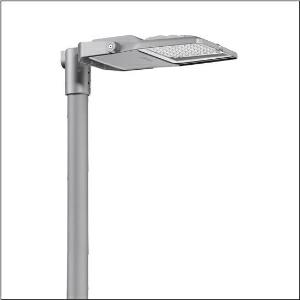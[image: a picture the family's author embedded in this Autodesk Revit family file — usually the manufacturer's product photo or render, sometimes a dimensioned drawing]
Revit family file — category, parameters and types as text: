
# Revit family: floodlight_fl_21_iq_mini___pl33t_5xa7772b4f3a_8cfb
name_source: partatom
category: Lighting Fixtures
units: mm (PartAtom-declared; Revit-internal decimal feet)

## family parameters
Cut with Voids When Loaded = No
Host = Face
Light Source = No
Part Type = Normal
Room Calculation Point = No
Round Connector Dimension = Use Diameter
Shared = No

## types (1)
- --- (1 x LED, 6420 lm, 45.5 W, 4000K)
    Apparent Load = 46 VA
    CIE Flux Codes = 26 75 99 100 100
    Color Rendering = 70
    Color Temperature = 4000K
    Default Elevation = 1800 mm
    Description = Floodlight FL 21 iQ mini, floodlight, primary light control with lens, of PMMA, primary optical cover: protective disc, of toughened safety glass, transparent, light distribution: PL33T, light emission: direct distribution, installation type: surface-mounted, LED, High Power LED, rated luminous flux: 6.420lm, luminous efficacy: 141lm/W, light colour: 740, colour temperature: 4000K, control: Auto-Match, Temp-Guard, Night-Set, Smart-Wire, Desk-Remote (wireless, voltage-free reading and setting of iQ features in the workshop via application-optimized NFC function/RFID function), optimised constant luminous flux control (CLO 2.0), Light-Fading, Lumen-Switch, with terminal, 6-pole, mains connection: 220..240V, AC, 50/60Hz, start of lifetime: 46W, end of service life: 48W, reduction: 22W, luminaire housing, of diecast aluminium, powder-coated, Siteco® metallic grey (DB 702S), corrosivity category C5 mid according to DIN EN ISO 12944, sealing non-destructively replaceable, please order mast flange separately, mast bracket, of steel, galvanised, powder-coated, protection rating (complete): IP66, insulation class (complete): insulation class II (safety insulation), certification: CE, ENEC, VDE, protection symbol: D, impact resistance: IK08, permissible operating ambient temperature: -40..+40°C, permissible operating ambient temperature for outdoor applications: -40..+50°C, standard: DIN EN 12944, LABS conformity tested according to VDMA 24364:2018-05, packaging unit: 1 piece

Light Distribution: PL33T
    Height = 70 mm
    Lamp = 1 x LED
    Lamp Light Flux = 6420 lm
    Lamp Power = 45.5 W
    Lamp count = 1
    Length = 485 mm
    Luminous efficacy = 141 lm/W
    Manufacturer = Siteco
    ModVariant = No
    Model = 5XA7772B4F3A
    Number of Poles = 1
    OnlyDefault = Yes
    Power Factor = 1
    Product Name = Floodlight FL 21 iQ mini | PL33T
    Product group = floodlight | pylon annexe
    ProductGroupID = 6200
    Protection Class = Protection class II
    Protection Degree = IP 66
    RLX_Detail_Level = 1
    RLX_Emergency_Light_Flux = 0 lm
    RLX_Emergency_Type = 0
    RLX_Emergency_Type_DB = No
    RlxData = <blob elided: 100989 chars, md5=b111217c>
    Socket = socket
    Standby Power = 0 W
    System Light Flux = 6420 lm
    System Power = 46 W
    Type Comments = factory setting: luminous flux: 100 % | dim-lin: 254 | 463 mA
    Type Image = l_1007125.jpg
    URL = http://relux.com
    VarID = @adj_120221
    Voltage = 0 V
    Weight = 0.00 kg
    Width = 337 mm

## geometry (parser evidence)
native form markers: Blend x4, Sweep x13
no freeform markers — native parametric forms only
